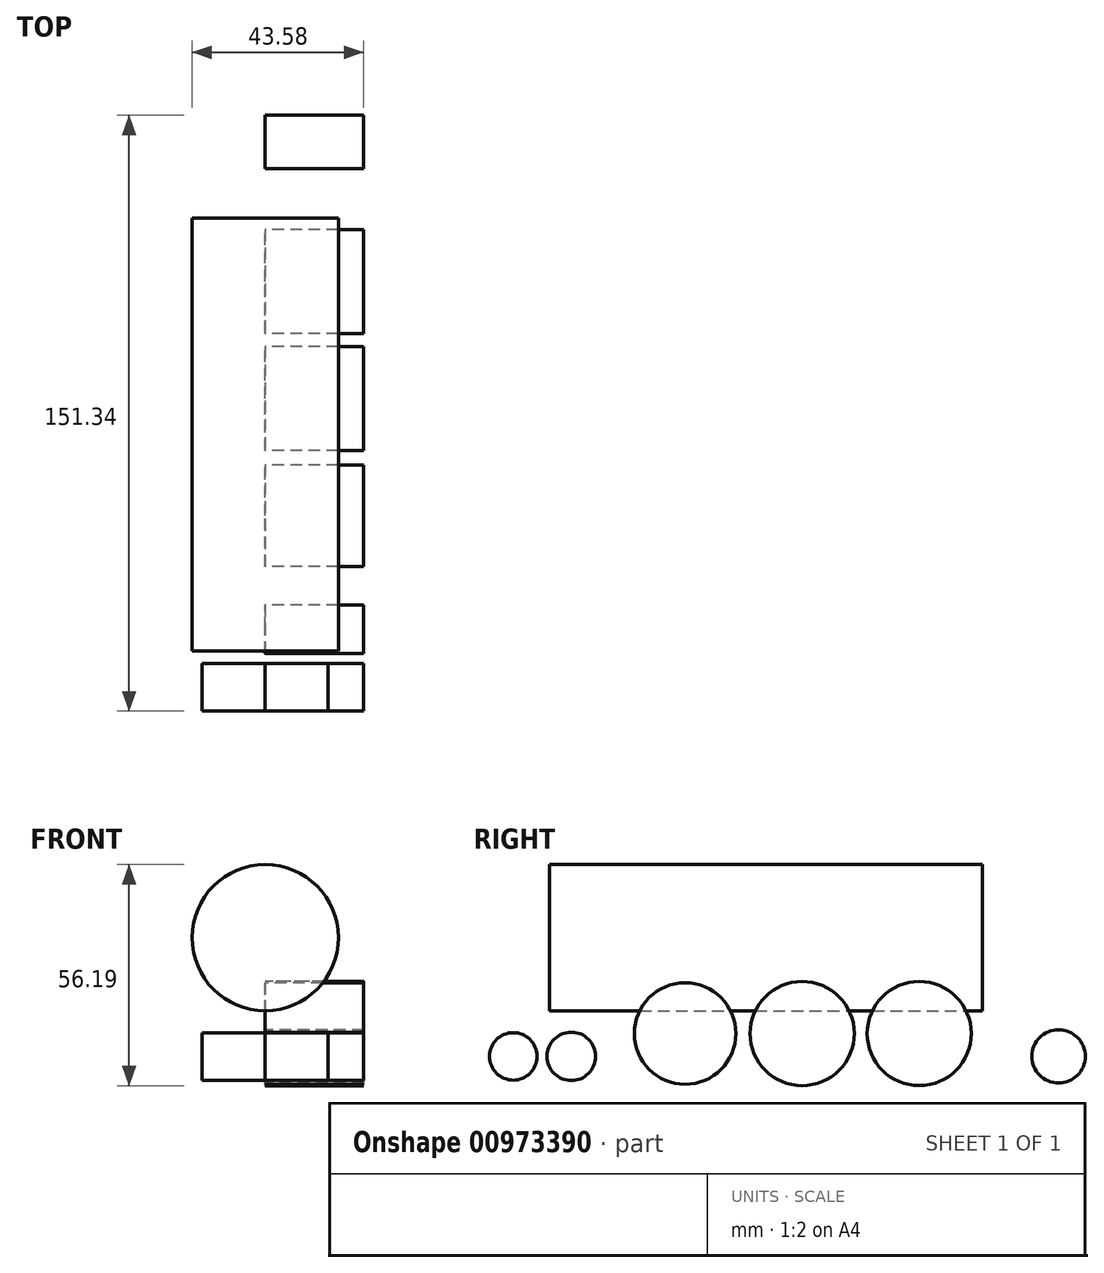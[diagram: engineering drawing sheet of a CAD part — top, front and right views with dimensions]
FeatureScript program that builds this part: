
annotation { "Feature Type Name" : "Feature", "Feature Type Description" : "" }
export const myFeature = defineFeature(function(context is Context, id is Id, definition is map)
    precondition{}
    {
        {
            var Q0;
            Q0=qCreatedBy(makeId("Right.planeOp"),FACE);
            var sketch = newSketch(context, id + "F0", { "sketchPlane" : qUnion([Q0])});
            skCircle(sketch, "E0", {"center": v(-64.16, 0) * mm, "radius": 6.03 * mm});
            skCircle(sketch, "E1", {"center": v(-49.43, 0) * mm, "radius": 6.15 * mm});
            skCircle(sketch, "E2", {"center": v(-20.54, 5.8) * mm, "radius": 12.9 * mm});
            skCircle(sketch, "E3", {"center": v(9.2, 5.8) * mm, "radius": 13.24 * mm});
            skCircle(sketch, "E4", {"center": v(38.95, 5.8) * mm, "radius": 13.22 * mm});
            skCircle(sketch, "E5", {"center": v(74.36, 0) * mm, "radius": 6.79 * mm});
            skSolve(sketch);
        }
        {
            var Q0;
            Q0=qCreatedBy(makeId("Front.planeOp"),FACE);
            var sketch = newSketch(context, id + "F1", { "sketchPlane" : qUnion([Q0])});
            skCircle(sketch, "E6", {"center": v(0, 30.17) * mm, "radius": 18.58 * mm});
            skSolve(sketch);
        }
        {
            var Q0;
            Q0=makeQuery(id+"F1.imprint","IMPRINT",FACE,{"disambiguationData":[TD([[makeQuery(id+"F1.imprint","IMPRINT",EDGE,{"derivedFrom":sQuery(id+"F1.wireOp",EDGE,"E6")}),1.0]])]});
            extrude(context, id + "F2", {"entities" : qUnion([Q0]), "depth" : 55 * mm, "offsetDistance" : 25 * mm, "hasSecondDirection" : true, "secondDirectionOppositeDirection" : true, "secondDirectionDepth" : 55 * mm});
        }
        {
            var Q0;
            Q0=makeQuery(id+"F0.imprint","IMPRINT",FACE,{"disambiguationData":[TD([[makeQuery(id+"F0.imprint","IMPRINT",EDGE,{"derivedFrom":sQuery(id+"F0.wireOp",EDGE,"E0")}),1.0]])]});
            extrude(context, id + "F3", {"entities" : qUnion([Q0]), "depth" : 16 * mm, "offsetDistance" : 25 * mm, "hasSecondDirection" : true, "secondDirectionOppositeDirection" : true, "secondDirectionDepth" : 16 * mm});
        }
        {
            var Q0;
            Q0 = qSketchRegion(id + "F0", true);
            extrude(context, id + "F4", {"entities" : qUnion([Q0]), "depth" : 25 * mm, "offsetDistance" : 25 * mm});
        }
    });
